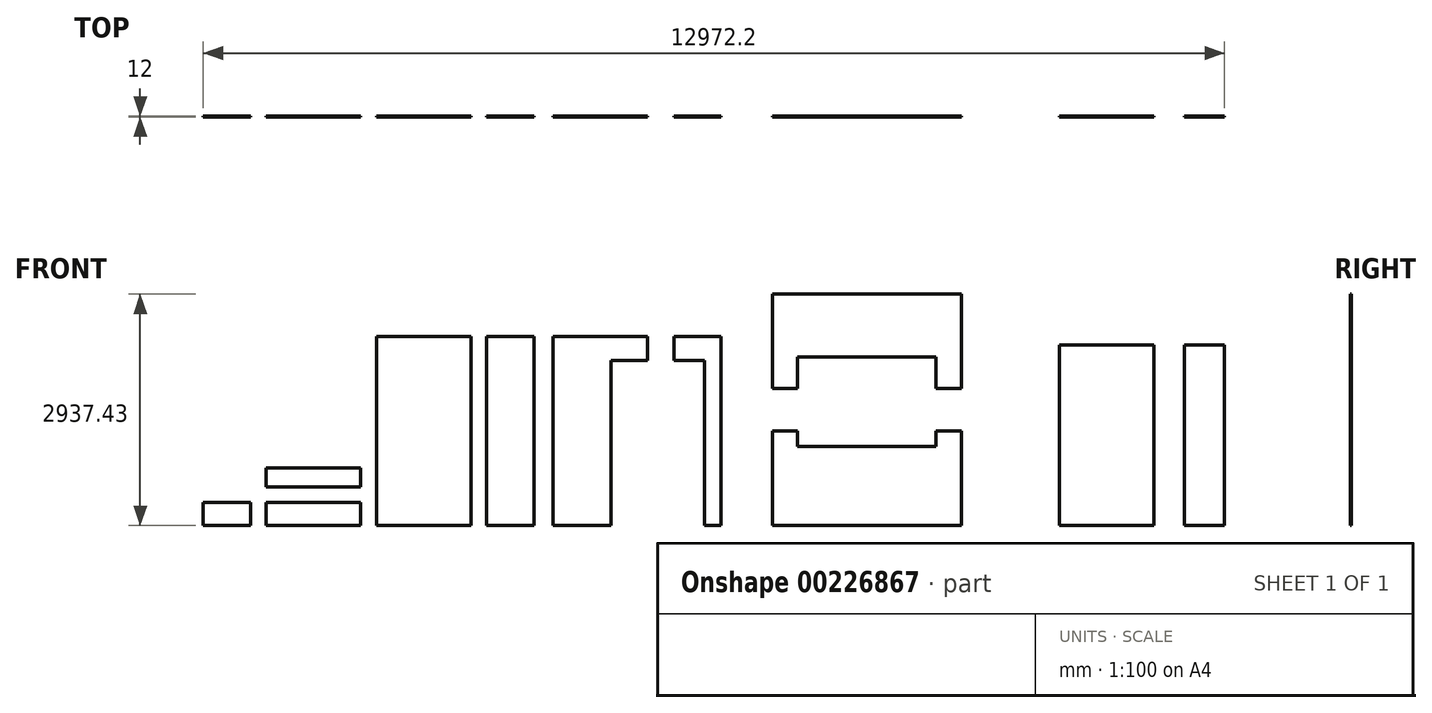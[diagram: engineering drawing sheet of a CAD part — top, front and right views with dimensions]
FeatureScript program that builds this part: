
annotation { "Feature Type Name" : "Feature", "Feature Type Description" : "" }
export const myFeature = defineFeature(function(context is Context, id is Id, definition is map)
    precondition{}
    {
        {
            var Q0;
            Q0=qCreatedBy(makeId("Front.planeOp"),FACE);
            var sketch = newSketch(context, id + "F0", { "sketchPlane" : qUnion([Q0])});
            skLineSegment(sketch, "E0.bottom", {"start": v(0, 0) * mm, "end": v(1200, 0) * mm});
            skLineSegment(sketch, "E0.top", {"start": v(0, 2400) * mm, "end": v(1200, 2400) * mm});
            skLineSegment(sketch, "E0.left", {"start": v(0, 0) * mm, "end": v(0, 2400) * mm});
            skLineSegment(sketch, "E0.right", {"start": v(1200, 0) * mm, "end": v(1200, 2400) * mm});
            skLineSegment(sketch, "E1.bottom", {"start": v(1400, 0) * mm, "end": v(2000, 0) * mm});
            skLineSegment(sketch, "E1.top", {"start": v(1400, 2400) * mm, "end": v(2000, 2400) * mm});
            skLineSegment(sketch, "E1.left", {"start": v(1400, 0) * mm, "end": v(1400, 2400) * mm});
            skLineSegment(sketch, "E1.right", {"start": v(2000, 0) * mm, "end": v(2000, 2400) * mm});
            skLineSegment(sketch, "E2.bottom", {"start": v(2241.64, 0) * mm, "end": v(2976.64, 0) * mm});
            skLineSegment(sketch, "E2.top", {"start": v(2241.64, 2400) * mm, "end": v(3441.64, 2400) * mm});
            skLineSegment(sketch, "E2.left", {"start": v(2241.64, 0) * mm, "end": v(2241.64, 2400) * mm});
            skLineSegment(sketch, "E2.right", {"start": v(3441.64, 2095) * mm, "end": v(3441.64, 2400) * mm});
            skLineSegment(sketch, "E3", {"start": v(3441.64, 2095) * mm, "end": v(2976.64, 2095) * mm});
            skLineSegment(sketch, "E4", {"start": v(2976.64, 2095) * mm, "end": v(2976.64, 0) * mm});
            skLineSegment(sketch, "E5.bottom", {"start": v(4164.08, 0) * mm, "end": v(4379.08, 0) * mm});
            skLineSegment(sketch, "E5.top", {"start": v(3779.08, 2400) * mm, "end": v(4379.08, 2400) * mm});
            skLineSegment(sketch, "E5.left", {"start": v(3779.08, 2095) * mm, "end": v(3779.08, 2400) * mm});
            skLineSegment(sketch, "E5.right", {"start": v(4379.08, 0) * mm, "end": v(4379.08, 2400) * mm});
            skLineSegment(sketch, "E6", {"start": v(3779.08, 2095) * mm, "end": v(4164.08, 2095) * mm});
            skLineSegment(sketch, "E7", {"start": v(4164.08, 2095) * mm, "end": v(4164.08, 0) * mm});
            skLineSegment(sketch, "E8.bottom", {"start": v(5029.04, 0) * mm, "end": v(7429.04, 0) * mm});
            skLineSegment(sketch, "E8.top", {"start": v(5029.04, 1200) * mm, "end": v(5349.04, 1200) * mm});
            skLineSegment(sketch, "E8.left", {"start": v(5029.04, 0) * mm, "end": v(5029.04, 1200) * mm});
            skLineSegment(sketch, "E8.right", {"start": v(7429.04, 0) * mm, "end": v(7429.04, 1200) * mm});
            skLineSegment(sketch, "E9", {"start": v(5349.04, 1200) * mm, "end": v(5349.04, 1000) * mm});
            skLineSegment(sketch, "E10", {"start": v(5349.04, 1000) * mm, "end": v(7109.04, 1000) * mm});
            skLineSegment(sketch, "E11", {"start": v(7109.04, 1000) * mm, "end": v(7109.04, 1200) * mm});
            skLineSegment(sketch, "E12.trimOffspring", {"start": v(7109.04, 1200) * mm, "end": v(7429.04, 1200) * mm});
            skLineSegment(sketch, "E13.bottom", {"start": v(5029.04, 1737.43) * mm, "end": v(5349.04, 1737.43) * mm});
            skLineSegment(sketch, "E13.top", {"start": v(5029.04, 2937.43) * mm, "end": v(7429.04, 2937.43) * mm});
            skLineSegment(sketch, "E13.left", {"start": v(5029.04, 1737.43) * mm, "end": v(5029.04, 2937.43) * mm});
            skLineSegment(sketch, "E13.right", {"start": v(7429.04, 1737.43) * mm, "end": v(7429.04, 2937.43) * mm});
            skLineSegment(sketch, "E14", {"start": v(5349.04, 1737.43) * mm, "end": v(5349.04, 2137.43) * mm});
            skLineSegment(sketch, "E15", {"start": v(5349.04, 2137.43) * mm, "end": v(7109.04, 2137.43) * mm});
            skLineSegment(sketch, "E16", {"start": v(7109.04, 2137.43) * mm, "end": v(7109.04, 1737.43) * mm});
            skLineSegment(sketch, "E17.trimOffspring", {"start": v(7109.04, 1737.43) * mm, "end": v(7429.04, 1737.43) * mm});
            skLineSegment(sketch, "E18.bottom", {"start": v(8678.63, 0) * mm, "end": v(9878.63, 0) * mm});
            skLineSegment(sketch, "E18.top", {"start": v(8678.63, 2295) * mm, "end": v(9878.63, 2295) * mm});
            skLineSegment(sketch, "E18.left", {"start": v(8678.63, 0) * mm, "end": v(8678.63, 2295) * mm});
            skLineSegment(sketch, "E18.right", {"start": v(9878.63, 0) * mm, "end": v(9878.63, 2295) * mm});
            skLineSegment(sketch, "E19.bottom", {"start": v(10262.16, 0) * mm, "end": v(10772.16, 0) * mm});
            skLineSegment(sketch, "E19.top", {"start": v(10262.16, 2295) * mm, "end": v(10772.16, 2295) * mm});
            skLineSegment(sketch, "E19.left", {"start": v(10262.16, 0) * mm, "end": v(10262.16, 2295) * mm});
            skLineSegment(sketch, "E19.right", {"start": v(10772.16, 0) * mm, "end": v(10772.16, 2295) * mm});
            skLineSegment(sketch, "E20.bottom", {"start": v(-200, 0) * mm, "end": v(-1400, 0) * mm});
            skLineSegment(sketch, "E20.top", {"start": v(-200, 290) * mm, "end": v(-1400, 290) * mm});
            skLineSegment(sketch, "E20.left", {"start": v(-200, 0) * mm, "end": v(-200, 290) * mm});
            skLineSegment(sketch, "E20.right", {"start": v(-1400, 0) * mm, "end": v(-1400, 290) * mm});
            skLineSegment(sketch, "E21.bottom", {"start": v(-1600, 0) * mm, "end": v(-2200, 0) * mm});
            skLineSegment(sketch, "E21.top", {"start": v(-1600, 290) * mm, "end": v(-2200, 290) * mm});
            skLineSegment(sketch, "E21.left", {"start": v(-1600, 0) * mm, "end": v(-1600, 290) * mm});
            skLineSegment(sketch, "E21.right", {"start": v(-2200, 0) * mm, "end": v(-2200, 290) * mm});
            skLineSegment(sketch, "E22.bottom", {"start": v(-200, 490) * mm, "end": v(-1400, 490) * mm});
            skLineSegment(sketch, "E22.top", {"start": v(-200, 730) * mm, "end": v(-1400, 730) * mm});
            skLineSegment(sketch, "E22.left", {"start": v(-200, 490) * mm, "end": v(-200, 730) * mm});
            skLineSegment(sketch, "E22.right", {"start": v(-1400, 490) * mm, "end": v(-1400, 730) * mm});
            skSolve(sketch);
        }
        {
            var Q0;
            Q0=makeQuery(id+"F0.imprint","IMPRINT",FACE,{"disambiguationData":[TD([[makeQuery(id+"F0.imprint","IMPRINT",EDGE,{"derivedFrom":sQuery(id+"F0.wireOp",EDGE,"E0.bottom")}),1.0]])]});
            var Q1;
            Q1=makeQuery(id+"F0.imprint","IMPRINT",FACE,{"disambiguationData":[TD([[makeQuery(id+"F0.imprint","IMPRINT",EDGE,{"derivedFrom":sQuery(id+"F0.wireOp",EDGE,"E1.bottom")}),1.0]])]});
            var Q2;
            Q2=makeQuery(id+"F0.imprint","IMPRINT",FACE,{"disambiguationData":[TD([[makeQuery(id+"F0.imprint","IMPRINT",EDGE,{"derivedFrom":sQuery(id+"F0.wireOp",EDGE,"E2.bottom")}),1.0]])]});
            var Q3;
            Q3=makeQuery(id+"F0.imprint","IMPRINT",FACE,{"disambiguationData":[TD([[makeQuery(id+"F0.imprint","IMPRINT",EDGE,{"derivedFrom":sQuery(id+"F0.wireOp",EDGE,"E5.bottom")}),1.0]])]});
            var Q4;
            Q4=makeQuery(id+"F0.imprint","IMPRINT",FACE,{"disambiguationData":[TD([[makeQuery(id+"F0.imprint","IMPRINT",EDGE,{"derivedFrom":sQuery(id+"F0.wireOp",EDGE,"E8.bottom")}),1.0]])]});
            var Q5;
            Q5=makeQuery(id+"F0.imprint","IMPRINT",FACE,{"disambiguationData":[TD([[makeQuery(id+"F0.imprint","IMPRINT",EDGE,{"derivedFrom":sQuery(id+"F0.wireOp",EDGE,"E13.bottom")}),1.0]])]});
            var Q6;
            Q6=makeQuery(id+"F0.imprint","IMPRINT",FACE,{"disambiguationData":[TD([[makeQuery(id+"F0.imprint","IMPRINT",EDGE,{"derivedFrom":sQuery(id+"F0.wireOp",EDGE,"E18.bottom")}),1.0]])]});
            var Q7;
            Q7=makeQuery(id+"F0.imprint","IMPRINT",FACE,{"disambiguationData":[TD([[makeQuery(id+"F0.imprint","IMPRINT",EDGE,{"derivedFrom":sQuery(id+"F0.wireOp",EDGE,"E19.bottom")}),1.0]])]});
            var Q8;
            Q8=makeQuery(id+"F0.imprint","IMPRINT",FACE,{"disambiguationData":[TD([[makeQuery(id+"F0.imprint","IMPRINT",EDGE,{"derivedFrom":sQuery(id+"F0.wireOp",EDGE,"E20.bottom")}),-1.0]])]});
            var Q9;
            Q9=makeQuery(id+"F0.imprint","IMPRINT",FACE,{"disambiguationData":[TD([[makeQuery(id+"F0.imprint","IMPRINT",EDGE,{"derivedFrom":sQuery(id+"F0.wireOp",EDGE,"E21.bottom")}),-1.0]])]});
            var Q10;
            Q10=makeQuery(id+"F0.imprint","IMPRINT",FACE,{"disambiguationData":[TD([[makeQuery(id+"F0.imprint","IMPRINT",EDGE,{"derivedFrom":sQuery(id+"F0.wireOp",EDGE,"E22.bottom")}),-1.0]])]});
            extrude(context, id + "F1", {"entities" : qUnion([Q0, Q1, Q2, Q3, Q4, Q5, Q6, Q7, Q8, Q9, Q10]), "oppositeDirection" : true, "depth" : 12 * mm});
        }
    });
